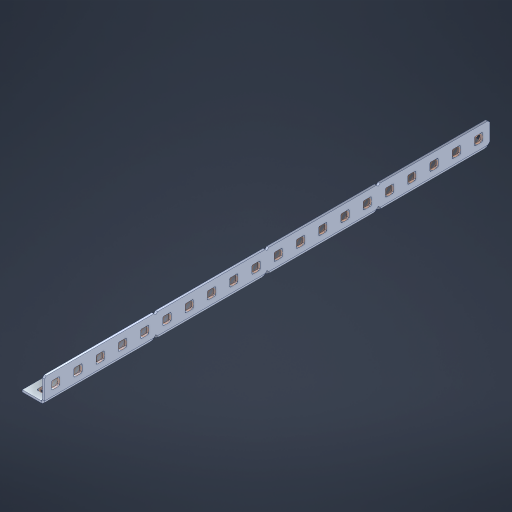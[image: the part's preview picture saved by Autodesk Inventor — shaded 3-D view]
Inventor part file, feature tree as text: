
AUTODESK INVENTOR PART (.ipt)
format: ipt  version: 2023 (Build 270158000, 158)  size: 757,248 bytes
history: native  units: in
note: dims shown in document units (in); Inventor stores cm internally (conversion verified against a paired STEP export)
features: other x45, extrude x39, sheet_metal_op x10, sketch x8, mirror x1, pattern_linear x1, chamfer x1
ambient origin geometry x8: Origin, YZ Plane, XZ Plane, XY Plane, X Axis, Y Axis, Z Axis, Center Point
bodies: Solid1 (feature_tree), Body (feature_tree)
feature tree (105):
  other  "Flange Pattern Plane"
  sheet_metal_op  "Flange Pattern"
  sheet_metal_op  "Body Pattern"
  other  "Arc Length"
  mirror  "Notch Mirror"
  pattern_linear  "Notch Pattern"  Spacing1=0.1875in  [1 undecoded]
  chamfer  "End Chamfer"
  extrude  "Half Cut"  Depth=0.0469in
  sketch  "Sketch1"  dims[d0=2.5in]
  other  "Plate1"
  sketch  "Sketch2"  dims[d1=10.0in]
  other  "Plate2"
  sheet_metal_op  "Bend1"
  sheet_metal_op  "Corner1"
  sketch  "Sketch3"  dims[d2=0.0469in]
  other  "Flange Pattern Sketch"
  sketch  "Sketch7"  dims[d3=0.0469in]
  other  "Srf1"
  other  "Srf2"
  sketch  "Sketch8"  dims[d4=0.0234in]
  sketch  "Sketch9"  dims[d5=0.0938in]
  other  "Srf91"
  sheet_metal_op  "Body Pattern Sketch"
  other  "Srf92"
  sketch  "Sketch13"  dims[d6=0.0469in]
  sketch  "Sketch14"  dims[d7=0.5in d8=90.0deg d9=0.0312in d10=0.1875in d11=0.0469in d12=0.0469in d16=0.182in d17=0.02in d18=0.0469in d19=0.0in d20=0.25in d21=0.25in d46=0.172in d47=1.0in d48=0.0in d49=0.182in d50=0.02in d51=0.25in d52=0.25in d53=0.0469in d54=0.0in d55=0.172in d56=1.0in d57=0.0in d60=7.874in d62=0.5in d63=0.3937in d65=0.5in d85=0.1227in d86=0.1659in d88=0.04in d89=0.0469in d90=0.0in d91=0.04in d92=0.0491in d95=2.5in d96=0.04in d97=0.25in d98=45.0deg d101=0.0in d102=2.497in d131=0.5in d132=7.874in d134=0.5in d139=0.5in]
  other  "Srf856"
  other  "Srf1310"
  other  "Srf1311"
  other  "Srf1312"
  other  "Srf1376"
  other  "Srf1377"
  other  "Srf1728"
  other  "Srf1755"
  other  "Srf1878"
  other  "Srf1879"
  other  "Srf1880"
  other  "Srf1881"
  other  "Srf1882"
  other  "Srf1883"
  other  "Srf1884"
  other  "Srf1885"
  other  "Srf1886"
  other  "Srf1887"
  other  "Srf1888"
  other  "Srf1889"
  other  "Srf1890"
  other  "Srf1891"
  other  "Srf1942"
  other  "Srf1943"
  other  "Srf1944"
  other  "Srf1945"
  other  "Srf1946"
  other  "Srf1947"
  other  "Srf1948"
  other  "Srf1949"
  other  "Srf1950"
  other  "Srf1951"
  other  "Srf1952"
  other  "Srf1953"
  other  "Srf1954"
  other  "Srf1955"
  sheet_metal_op  "Flange Stamp"
  sheet_metal_op  "Flange Circle"
  sheet_metal_op  "Body Stamp"
  sheet_metal_op  "Body Circle"
  sheet_metal_op  "Notch"
  extrude  "ExtrusionSrf2"  Depth=0.0469in
  extrude  "ExtrusionSrf92"  Depth=0.5in
  extrude  "ExtrusionSrf856"  Depth=0.02in
  extrude  "ExtrusionSrf1310"  Depth=0.0469in
  extrude  "ExtrusionSrf1311"  TaperAngle=0.0deg  [1 undecoded]
  extrude  "ExtrusionSrf1312"  Depth=0.5in
  extrude  "ExtrusionSrf1376"  Depth=0.5in
  extrude  "ExtrusionSrf1377"  Depth=0.5in
  extrude  "ExtrusionSrf1728"  Depth=0.5in TaperAngle=0.0deg
  extrude  "ExtrusionSrf1755"  Depth=0.5in
  extrude  "ExtrusionSrf1878"  Depth=0.02in
  extrude  "ExtrusionSrf1879"  Depth=0.5in
  extrude  "ExtrusionSrf1880"  Depth=0.5in
  extrude  "ExtrusionSrf1881"  Depth=0.0469in
  extrude  "ExtrusionSrf1882"  TaperAngle=0.0deg  [1 undecoded]
  extrude  "ExtrusionSrf1883"  Depth=0.5in
  extrude  "ExtrusionSrf1884"  Depth=0.5in TaperAngle=0.0deg
  extrude  "ExtrusionSrf1885"  Depth=0.5in
  extrude  "ExtrusionSrf1886"  Depth=0.5in
  extrude  "ExtrusionSrf1887"  Depth=0.5in
  extrude  "ExtrusionSrf1888"  Depth=0.5in
  extrude  "ExtrusionSrf1889"  Depth=0.5in
  extrude  "ExtrusionSrf1890"  Depth=0.0469in
  extrude  "ExtrusionSrf1891"  TaperAngle=0.0deg  [1 undecoded]
  extrude  "ExtrusionSrf1942"  Depth=0.5in
  extrude  "ExtrusionSrf1943"  Depth=0.5in
  extrude  "ExtrusionSrf1944"  Depth=0.5in
  extrude  "ExtrusionSrf1945"  Depth=0.5in TaperAngle=45.0deg
  extrude  "ExtrusionSrf1946"  TaperAngle=0.0deg  [1 undecoded]
  extrude  "ExtrusionSrf1947"  Depth=0.5in
  extrude  "ExtrusionSrf1948"  Depth=0.5in
  extrude  "ExtrusionSrf1949"  Depth=0.5in
  extrude  "ExtrusionSrf1950"  Depth=0.5in
  extrude  "ExtrusionSrf1951"  Depth=0.5in
  extrude  "ExtrusionSrf1952"  [1 undecoded]
  extrude  "ExtrusionSrf1953"  [1 undecoded]
  extrude  "ExtrusionSrf1954"  [1 undecoded]
  extrude  "ExtrusionSrf1955"  [1 undecoded]
note: 9 required parameter values undecoded (feature->parameter linkage not recoverable at this tier; creation-order binding heuristic only, values carry confidence <= 0.55)
